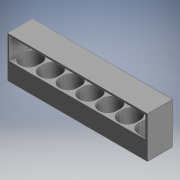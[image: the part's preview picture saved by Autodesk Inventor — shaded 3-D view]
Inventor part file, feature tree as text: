
AUTODESK INVENTOR PART (.ipt)
format: ipt  version: 2018 (Build 220112000, 112)  size: 165,376 bytes
history: native  units: in
note: dims shown in document units (in); Inventor stores cm internally (conversion verified against a paired STEP export)
features: extrude x3, other x2, pattern_linear x1, projected_geometry x1
ambient origin geometry x8: Origin, YZ Plane, XZ Plane, XY Plane, X Axis, Y Axis, Z Axis, Center Point
bodies: Solid1 (feature_tree)
feature tree (7):
  other  "Base Sketch"
  extrude  "Walls"  Depth=0.5512in TaperAngle=0.0deg
  extrude  "Back"  Depth=0.0394in
  extrude  "Whistle Hole"  Depth=0.0394in
  pattern_linear  "Rectangular Pattern2"  Spacing1=0.0394in  [1 undecoded]
  other  "Whistle Hole Sketch"
  projected_geometry  "Projected Loop1"
note: 1 required parameter value undecoded (feature->parameter linkage not recoverable at this tier; creation-order binding heuristic only, values carry confidence <= 0.55)
